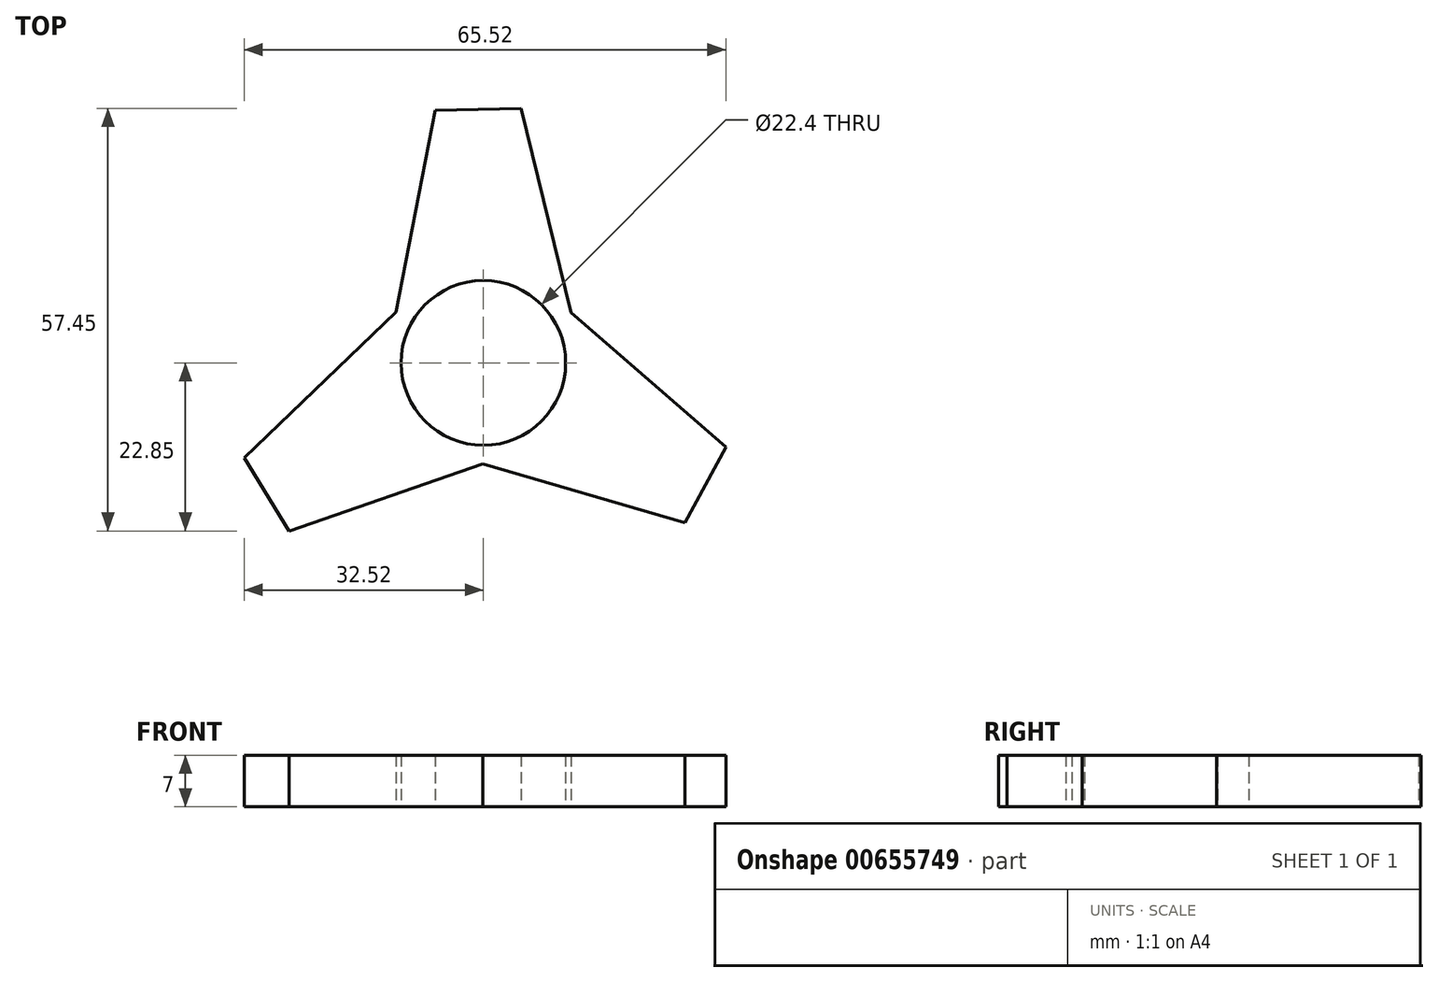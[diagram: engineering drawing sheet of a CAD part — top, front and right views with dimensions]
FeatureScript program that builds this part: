
annotation { "Feature Type Name" : "Feature", "Feature Type Description" : "" }
export const myFeature = defineFeature(function(context is Context, id is Id, definition is map)
    precondition{}
    {
        {
            var Q0;
            Q0=qCreatedBy(makeId("Top.planeOp"),FACE);
            var sketch = newSketch(context, id + "F0", { "sketchPlane" : qUnion([Q0])});
            skCircle(sketch, "E0", {"center": v(0, 0) * mm, "radius": 11.2 * mm});
            skLineSegment(sketch, "E1", {"start": v(5.11, 34.6) * mm, "end": v(11.92, 6.82) * mm});
            skLineSegment(sketch, "E2", {"start": v(-11.86, 6.91) * mm, "end": v(-6.57, 34.31) * mm});
            skLineSegment(sketch, "E3", {"start": v(-6.57, 34.31) * mm, "end": v(5.11, 34.6) * mm});
            skPoint(sketch, "E4.end.orphan", {"position": v(0, -13.2) * mm});
            skLineSegment(sketch, "E5.1.0", {"start": v(-26.43, -22.85) * mm, "end": v(-32.52, -12.88) * mm});
            skLineSegment(sketch, "E5.1.1", {"start": v(1.87, -13.07) * mm, "end": v(-26.43, -22.85) * mm});
            skLineSegment(sketch, "E5.1.2", {"start": v(-32.52, -12.88) * mm, "end": v(-11.86, 6.91) * mm});
            skLineSegment(sketch, "E5.2.0", {"start": v(33, -11.47) * mm, "end": v(27.41, -21.73) * mm});
            skLineSegment(sketch, "E5.2.1", {"start": v(11.92, 6.82) * mm, "end": v(33, -11.47) * mm});
            skLineSegment(sketch, "E5.2.2", {"start": v(27.41, -21.73) * mm, "end": v(-0.06, -13.73) * mm});
            skPoint(sketch, "E6.orphan", {"position": v(6.6, 11.43) * mm});
            skPoint(sketch, "E7.trimOffspring.end.orphan", {"position": v(13.6, 0) * mm});
            skPoint(sketch, "E8.orphan", {"position": v(-6.8, 11.77) * mm});
            skArc(sketch, "E9.trimOffspring", {"start": v(0, -13.2) * mm, "mid": v(0.94, -13.17) * mm, "end": v(1.87, -13.07) * mm});
            skPoint(sketch, "E10.orphan", {"position": v(-13.2, 0) * mm});
            skPoint(sketch, "E11.orphan", {"position": v(-6.8, -11.77) * mm});
            skPoint(sketch, "E12.orphan", {"position": v(6.6, -11.43) * mm});
            skSolve(sketch);
        }
        {
            var Q0;
            Q0 = qSketchRegion(id + "F0", true);
            extrude(context, id + "F1", {"entities" : qUnion([Q0]), "depth" : 7 * mm, "offsetDistance" : 25 * mm});
        }
    });
